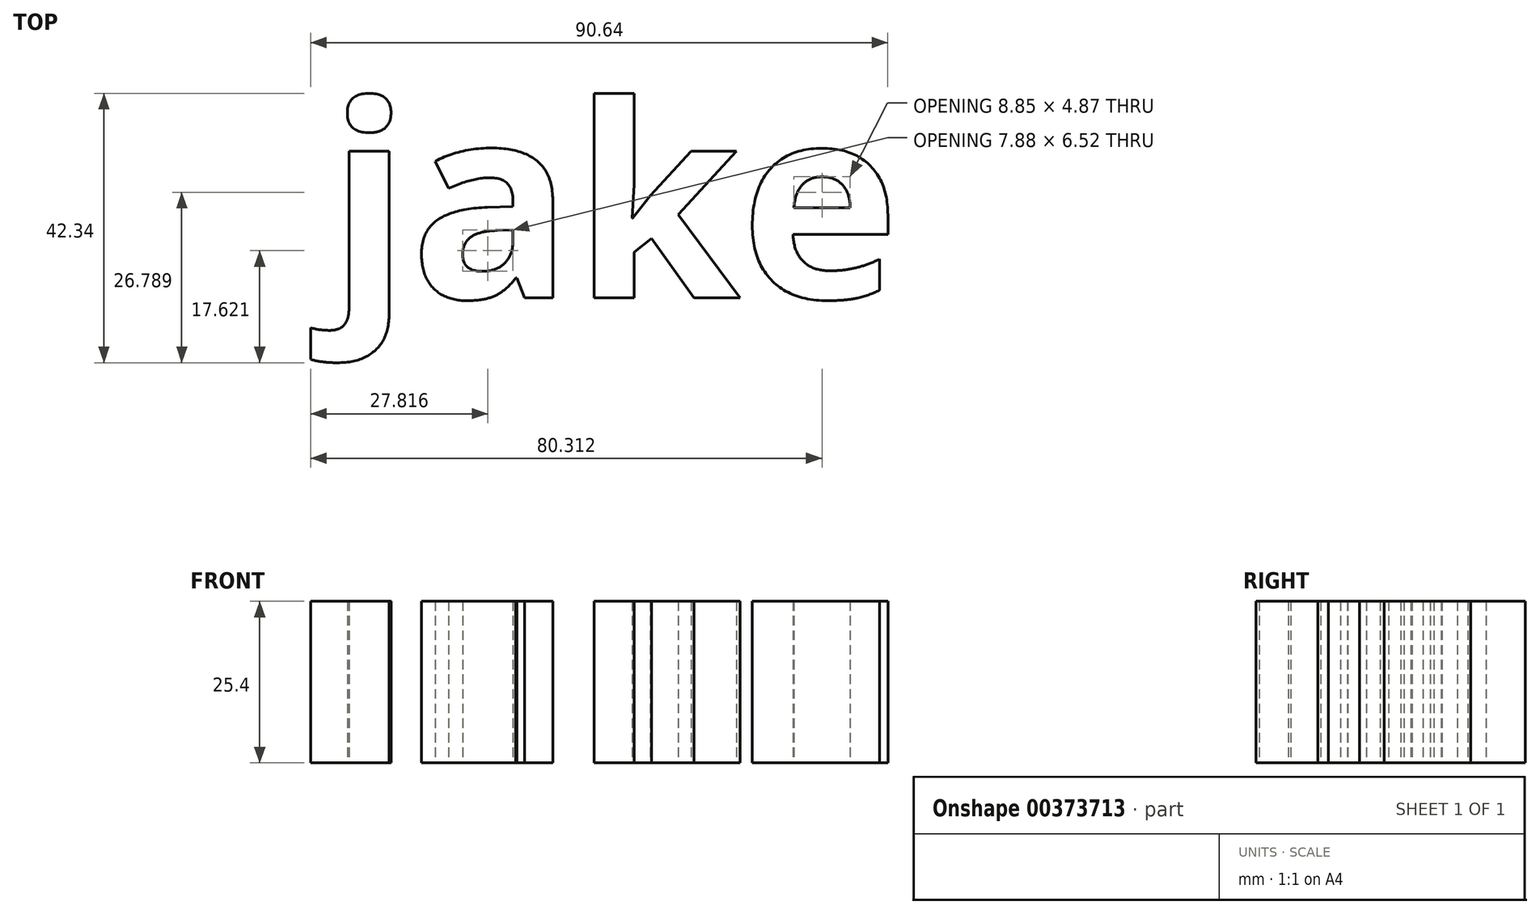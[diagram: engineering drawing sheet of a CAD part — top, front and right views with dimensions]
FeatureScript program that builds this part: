
annotation { "Feature Type Name" : "Feature", "Feature Type Description" : "" }
export const myFeature = defineFeature(function(context is Context, id is Id, definition is map)
    precondition{}
    {
        {
            var Q0;
            Q0=qCreatedBy(makeId("Top.planeOp"),FACE);
            var sketch = newSketch(context, id + "F0", { "sketchPlane" : qUnion([Q0])});
            skText(sketch, "E0", { "text": "jake", "fontName": "OpenSans-Bold.ttf"});
            const initialGuessF0  = {"E0": [-0.02652, -0.00442, 1, 0, 0.03048]};
            skSetInitialGuess(sketch, initialGuessF0);
            skSolve(sketch);
        }
        {
            var Q0;
            Q0 = qSketchRegion(id + "F0", true);
            extrude(context, id + "F1", {"entities" : qUnion([Q0]), "depth" : 25.4 * mm});
        }
    });
